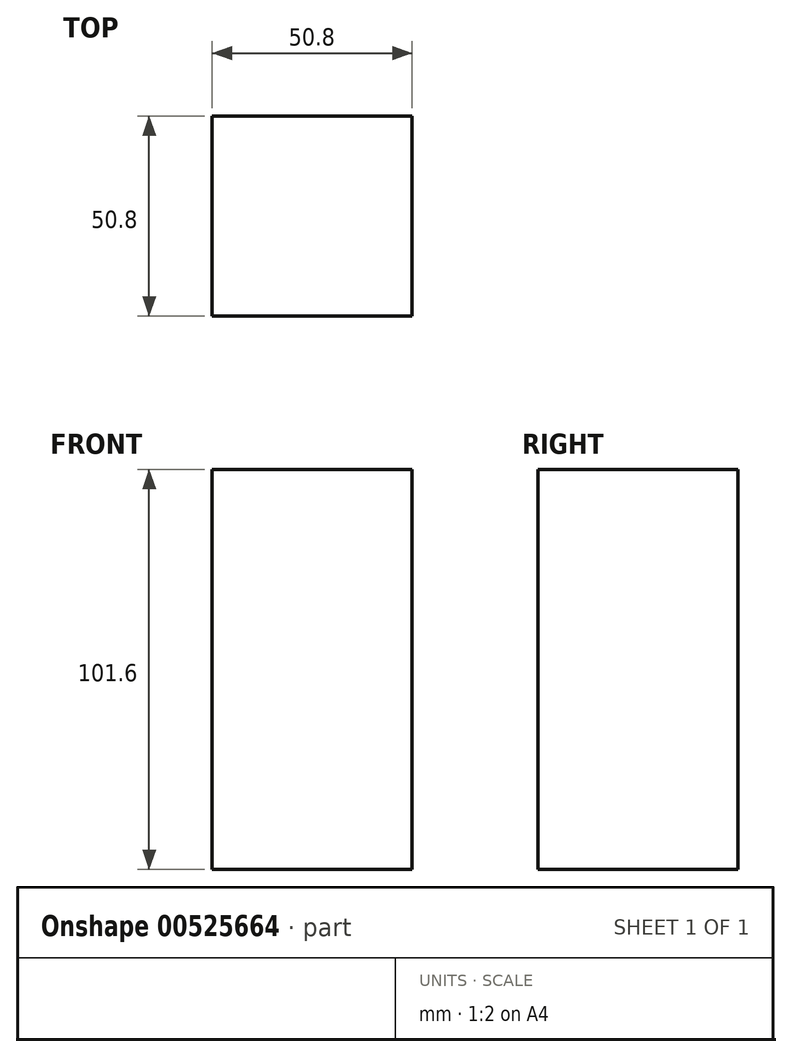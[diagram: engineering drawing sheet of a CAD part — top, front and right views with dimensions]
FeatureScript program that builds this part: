
annotation { "Feature Type Name" : "Feature", "Feature Type Description" : "" }
export const myFeature = defineFeature(function(context is Context, id is Id, definition is map)
    precondition{}
    {
        {
            var Q0;
            Q0=qCreatedBy(makeId("Top.planeOp"),FACE);
            var sketch = newSketch(context, id + "F0", { "sketchPlane" : qUnion([Q0])});
            skLineSegment(sketch, "E0.bottom", {"start": v(-25.4, 25.4) * mm, "end": v(25.4, 25.4) * mm});
            skLineSegment(sketch, "E0.top", {"start": v(-25.4, -25.4) * mm, "end": v(25.4, -25.4) * mm});
            skLineSegment(sketch, "E0.left", {"start": v(-25.4, 25.4) * mm, "end": v(-25.4, -25.4) * mm});
            skLineSegment(sketch, "E0.right", {"start": v(25.4, 25.4) * mm, "end": v(25.4, -25.4) * mm});
            skPoint(sketch, "E0.middle", {"position": v(0, 0) * mm});
            skSolve(sketch);
        }
        {
            var Q0;
            Q0 = qSketchRegion(id + "F0", true);
            extrude(context, id + "F1", {"entities" : qUnion([Q0]), "depth" : 50.8 * mm, "offsetDistance" : 25.4 * mm});
        }
        {
            var Q0;
            Q0=makeQuery(id+"F1.opExtrude","CAP_FACE",FACE,{"disambiguationData":[OSD([sQuery(id+"F0.wireOp",EDGE,"E0.bottom"),sQuery(id+"F0.wireOp",EDGE,"E0.top"),sQuery(id+"F0.wireOp",EDGE,"E0.left"),sQuery(id+"F0.wireOp",EDGE,"E0.right")])],"isStart":false});
            extrude(context, id + "F2", {"entities" : qUnion([Q0]), "operationType" : NewBodyOperationType.ADD, "depth" : 50.8 * mm, "offsetDistance" : 25.4 * mm});
        }
    });
